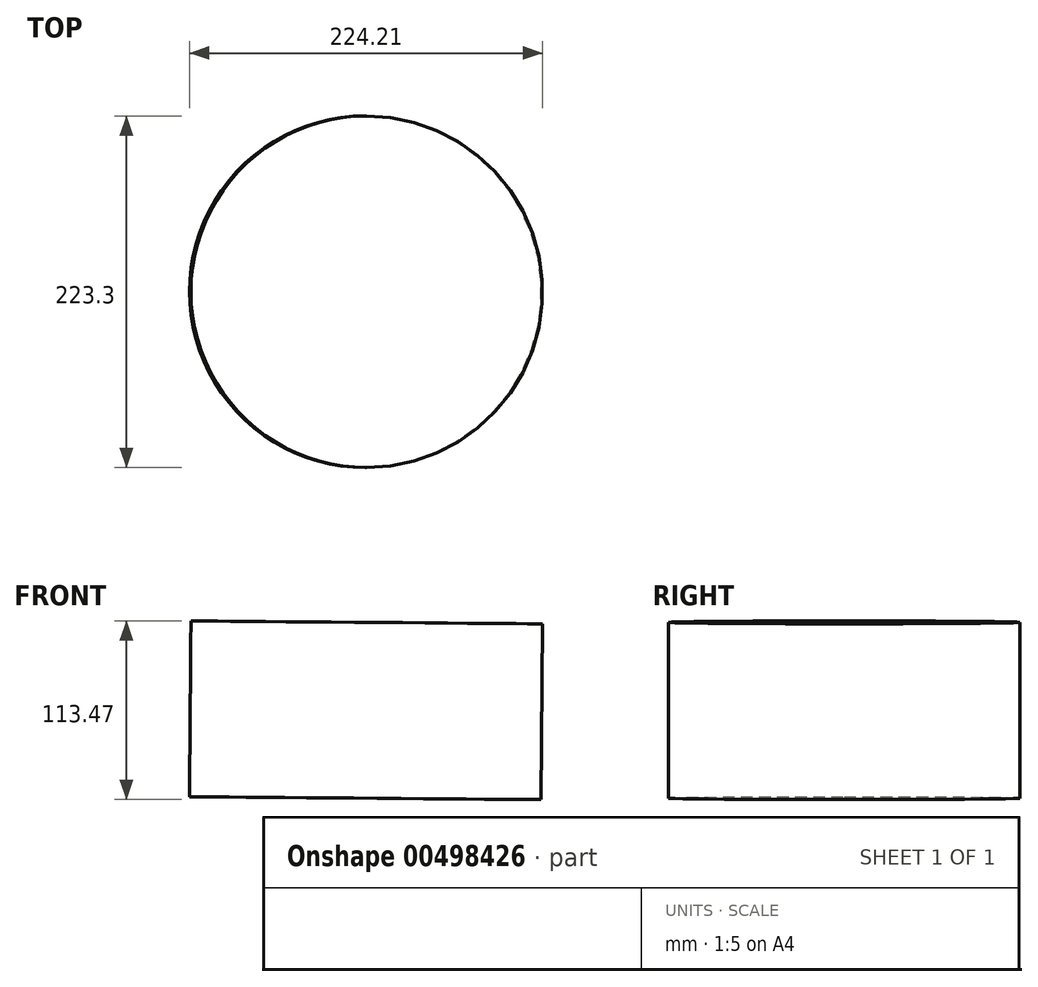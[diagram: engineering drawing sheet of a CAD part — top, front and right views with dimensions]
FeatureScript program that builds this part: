
annotation { "Feature Type Name" : "Feature", "Feature Type Description" : "" }
export const myFeature = defineFeature(function(context is Context, id is Id, definition is map)
    precondition{}
    {
        {
            var Q0;
            Q0=qCreatedBy(makeId("Front.planeOp"),FACE);
            var sketch = newSketch(context, id + "F0", { "sketchPlane" : qUnion([Q0])});
            skCircle(sketch, "E0.cCircle", {"center": v(0, 0) * mm, "radius": 78.95 * mm, "construction": true});
            skLineSegment(sketch, "E0.0", {"start": v(56.28, 55.37) * mm, "end": v(55.37, -56.28) * mm});
            skLineSegment(sketch, "E0.1", {"start": v(55.37, -56.28) * mm, "end": v(-56.28, -55.37) * mm});
            skLineSegment(sketch, "E0.2", {"start": v(-56.28, -55.37) * mm, "end": v(-55.37, 56.28) * mm});
            skLineSegment(sketch, "E0.3", {"start": v(-55.37, 56.28) * mm, "end": v(56.28, 55.37) * mm});
            skSolve(sketch);
        }
        {
            var Q0;
            Q0=makeQuery(id+"F0.imprint","IMPRINT",FACE,{"disambiguationData":[TD([[makeQuery(id+"F0.imprint","IMPRINT",EDGE,{"derivedFrom":sQuery(id+"F0.wireOp",EDGE,"E0.0")}),-1.0]])]});
            var Q1;
            Q1=sQuery(id+"F0.wireOp",EDGE,"E0.2");
            revolve(context, id + "F1", {"entities" : qUnion([Q0]), "axis" : qUnion([Q1]), "revolveType" : RevolveType.FULL});
        }
    });
